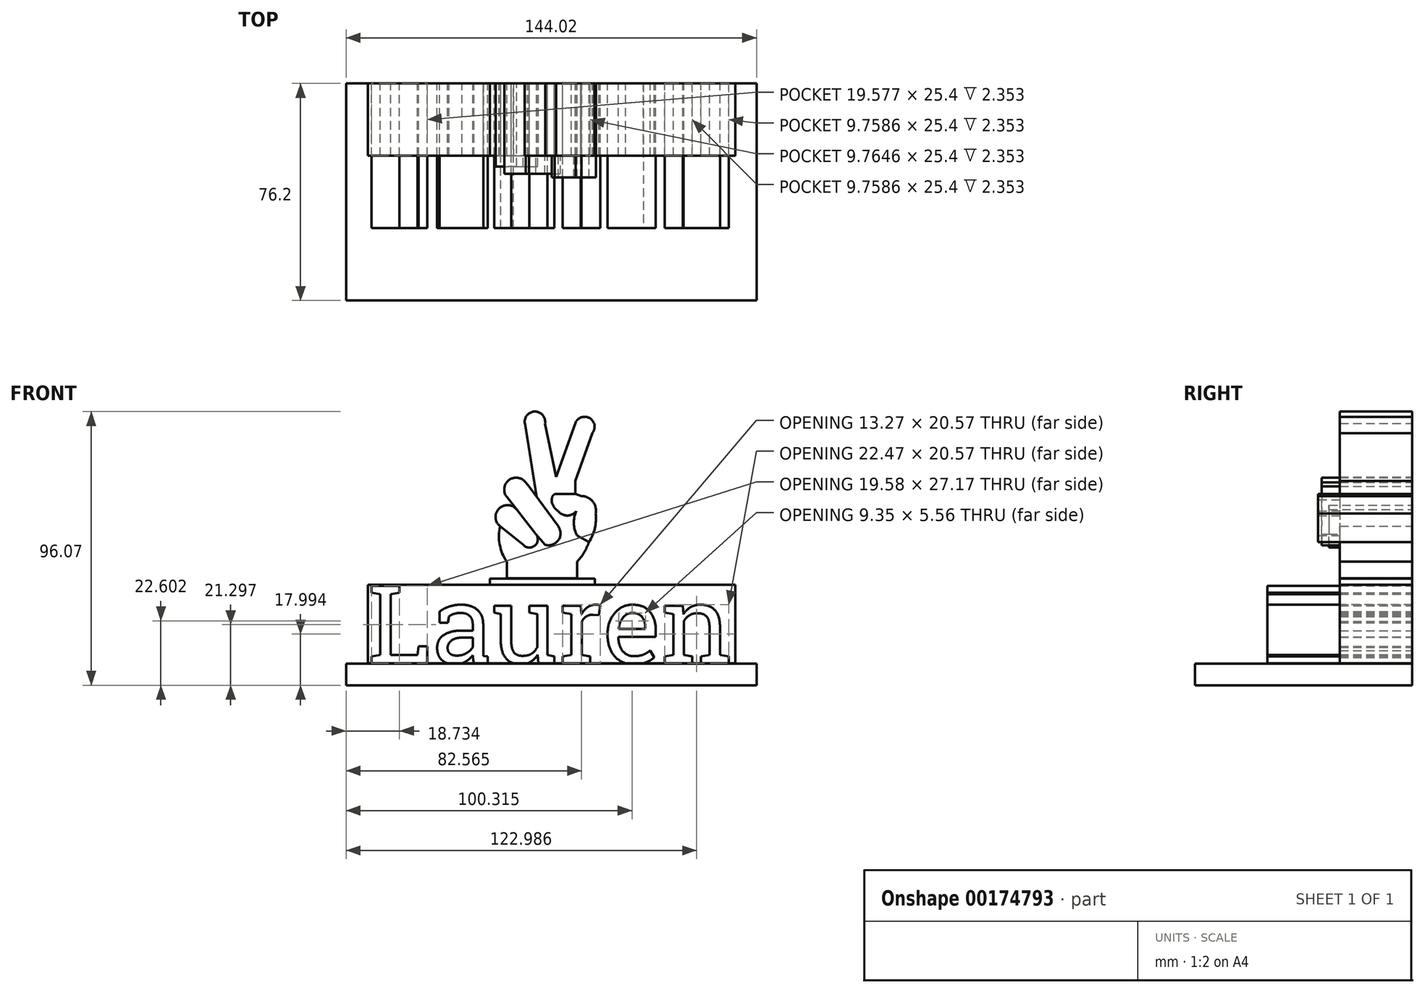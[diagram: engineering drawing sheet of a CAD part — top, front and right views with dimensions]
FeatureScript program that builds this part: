
annotation { "Feature Type Name" : "Feature", "Feature Type Description" : "" }
export const myFeature = defineFeature(function(context is Context, id is Id, definition is map)
    precondition{}
    {
        {
            var Q0;
            Q0=qCreatedBy(makeId("Front.planeOp"),FACE);
            var sketch = newSketch(context, id + "F0", { "sketchPlane" : qUnion([Q0])});
            skLineSegment(sketch, "E0.bottom", {"start": v(64.49, 13.76) * mm, "end": v(-64.49, 13.76) * mm});
            skLineSegment(sketch, "E0.top", {"start": v(64.49, -13.76) * mm, "end": v(-64.49, -13.76) * mm});
            skLineSegment(sketch, "E0.left", {"start": v(64.49, 13.76) * mm, "end": v(64.49, -13.76) * mm});
            skLineSegment(sketch, "E0.right", {"start": v(-64.49, 13.76) * mm, "end": v(-64.49, -13.76) * mm});
            skPoint(sketch, "E0.middle", {"position": v(0, 0) * mm});
            skText(sketch, "E1", { "text": "Lauren", "fontName": "RobotoSlab-Regular.ttf"});
            const initialGuessF0  = {"E1": [-0.06449, -0.01376, 1, 0, 0.02752]};
            skSetInitialGuess(sketch, initialGuessF0);
            skSolve(sketch);
        }
        {
            var Q0;
            Q0=makeQuery(id+"F0.imprint","IMPRINT",FACE,{"disambiguationData":[TD([[makeQuery(id+"F0.imprint","IMPRINT",EDGE,{"derivedFrom":sQuery(id+"F0.wireOp",EDGE,"E1.sketch_text.stroke-0")}),-1.0]])]});
            var Q1;
            Q1=makeQuery(id+"F0.imprint","IMPRINT",FACE,{"disambiguationData":[TD([[makeQuery(id+"F0.imprint","IMPRINT",EDGE,{"derivedFrom":sQuery(id+"F0.wireOp",EDGE,"E1.sketch_text.stroke-16")}),-1.0]])]});
            var Q2;
            {var subQ5=sQuery(id+"F0.wireOp",EDGE,"E1.sketch_text.stroke-51");Q2=makeQuery(id+"F0.imprint","IMPRINT",FACE,{"disambiguationData":[TD([[makeQuery(id+"F0.imprint","IMPRINT",EDGE,{"derivedFrom":subQ5}),-1.0]])]});}
            var Q3;
            Q3=makeQuery(id+"F0.imprint","IMPRINT",FACE,{"disambiguationData":[TD([[makeQuery(id+"F0.imprint","IMPRINT",EDGE,{"derivedFrom":sQuery(id+"F0.wireOp",EDGE,"E1.sketch_text.stroke-75")}),-1.0]])]});
            var Q4;
            {var subQ4=sQuery(id+"F0.wireOp",EDGE,"E1.sketch_text.stroke-95");Q4=makeQuery(id+"F0.imprint","IMPRINT",FACE,{"disambiguationData":[TD([[makeQuery(id+"F0.imprint","IMPRINT",EDGE,{"derivedFrom":subQ4}),-1.0]])]});}
            var Q5;
            Q5=makeQuery(id+"F0.imprint","IMPRINT",FACE,{"disambiguationData":[TD([[makeQuery(id+"F0.imprint","IMPRINT",EDGE,{"derivedFrom":sQuery(id+"F0.wireOp",EDGE,"E1.sketch_text.stroke-118")}),-1.0]])]});
            extrude(context, id + "F1", {"entities" : qUnion([Q0, Q1, Q2, Q3, Q4, Q5]), "depth" : 50.8 * mm});
        }
        {
            var Q0;
            Q0=makeQuery(id+"F0.imprint","IMPRINT",FACE,{"disambiguationData":[TD([[makeQuery(id+"F0.imprint","IMPRINT",EDGE,{"derivedFrom":sQuery(id+"F0.wireOp",EDGE,"E0.bottom")}),1.0]])]});
            extrude(context, id + "F2", {"entities" : qUnion([Q0]), "depth" : 25.4 * mm});
        }
        {
            var Q0;
            Q0=qCreatedBy(makeId("Front.planeOp"),FACE);
            var sketch = newSketch(context, id + "F3", { "sketchPlane" : qUnion([Q0])});
            skLineSegment(sketch, "E2", {"start": v(-15.98, 16.07) * mm, "end": v(8.98, 16.07) * mm});
            skLineSegment(sketch, "E3", {"start": v(8.98, 16.07) * mm, "end": v(8.98, 21.88) * mm});
            skLineSegment(sketch, "E4", {"start": v(-15.75, 21.88) * mm, "end": v(-15.75, 16.07) * mm});
            skArc(sketch, "E5", {"start": v(-18.1, 34.33) * mm, "mid": v(-18.2, 27.87) * mm, "end": v(-15.75, 21.88) * mm});
            skArc(sketch, "E6", {"start": v(-12.22, 40.18) * mm, "mid": v(-18.44, 40.55) * mm, "end": v(-18.1, 34.33) * mm});
            skLineSegment(sketch, "E7", {"start": v(-18.1, 34.33) * mm, "end": v(-10.02, 27.87) * mm});
            skPoint(sketch, "E7.endSnap0", {"position": v(-18.2, 27.87) * mm});
            skLineSegment(sketch, "E8", {"start": v(-12.22, 40.18) * mm, "end": v(-5.48, 31.62) * mm});
            skArc(sketch, "E9", {"start": v(-10.02, 27.87) * mm, "mid": v(-5.92, 27.53) * mm, "end": v(-5.48, 31.62) * mm});
            skLineSegment(sketch, "E10", {"start": v(-12.22, 40.18) * mm, "end": v(-15.75, 44.65) * mm});
            skArc(sketch, "E11", {"start": v(-9.15, 49.75) * mm, "mid": v(-15.02, 50.53) * mm, "end": v(-15.75, 44.65) * mm});
            skLineSegment(sketch, "E12", {"start": v(-7.95, 48.38) * mm, "end": v(2.3, 34.34) * mm});
            skLineSegment(sketch, "E13", {"start": v(-7.95, 48.38) * mm, "end": v(-9.15, 49.75) * mm});
            skLineSegment(sketch, "E14", {"start": v(-5.48, 31.62) * mm, "end": v(-2.4, 27.87) * mm});
            skArc(sketch, "E15", {"start": v(-2.4, 27.87) * mm, "mid": v(2.31, 29.39) * mm, "end": v(2.3, 34.34) * mm});
            skArc(sketch, "E16", {"start": v(8.72, 39.66) * mm, "mid": v(7.78, 35.36) * mm, "end": v(8.98, 31.12) * mm});
            skArc(sketch, "E17", {"start": v(2.3, 39.66) * mm, "mid": v(5.51, 38.1) * mm, "end": v(8.72, 39.66) * mm});
            skArc(sketch, "E18", {"start": v(0, 43.6) * mm, "mid": v(0.66, 41.34) * mm, "end": v(2.3, 39.66) * mm});
            skArc(sketch, "E19", {"start": v(1.05, 45.65) * mm, "mid": v(0.3, 44.74) * mm, "end": v(0, 43.6) * mm});
            skLineSegment(sketch, "E20", {"start": v(1.05, 45.65) * mm, "end": v(8.46, 45.65) * mm});
            skLineSegment(sketch, "E21", {"start": v(-5.3, 44.75) * mm, "end": v(-9.4, 70.44) * mm});
            skArc(sketch, "E22", {"start": v(-2.3, 70.44) * mm, "mid": v(-5.86, 74.6) * mm, "end": v(-9.4, 70.44) * mm});
            skLineSegment(sketch, "E23", {"start": v(-2.3, 70.44) * mm, "end": v(1.62, 51.63) * mm});
            skLineSegment(sketch, "E24", {"start": v(1.62, 51.63) * mm, "end": v(8.3, 70.44) * mm});
            skArc(sketch, "E25", {"start": v(14.28, 67.02) * mm, "mid": v(13.33, 72.3) * mm, "end": v(8.3, 70.44) * mm});
            skLineSegment(sketch, "E26", {"start": v(14.28, 67.02) * mm, "end": v(8.31, 50.2) * mm});
            skLineSegment(sketch, "E27", {"start": v(8.31, 50.2) * mm, "end": v(8.31, 45.65) * mm});
            skArc(sketch, "E28", {"start": v(8.98, 21.88) * mm, "mid": v(11.37, 25.1) * mm, "end": v(13.08, 28.72) * mm});
            skArc(sketch, "E29", {"start": v(13.08, 28.72) * mm, "mid": v(15.15, 33.56) * mm, "end": v(15.47, 38.8) * mm});
            skArc(sketch, "E30", {"start": v(15.47, 38.8) * mm, "mid": v(14.41, 43.03) * mm, "end": v(10.51, 44.96) * mm});
            skLineSegment(sketch, "E31", {"start": v(10.51, 44.96) * mm, "end": v(8.46, 45.65) * mm});
            skLineSegment(sketch, "E32", {"start": v(8.98, 31.12) * mm, "end": v(13.08, 28.72) * mm});
            skSolve(sketch);
        }
        {
            var Q0;
            {var subQ6=sQuery(id+"F3.wireOp",EDGE,"E3");Q0=makeQuery(id+"F3.imprint","IMPRINT",FACE,{"disambiguationData":[TD([[makeQuery(id+"F3.imprint","IMPRINT",EDGE,{"derivedFrom":subQ6}),1.0]])]});}
            extrude(context, id + "F4", {"entities" : qUnion([Q0]), "depth" : 25.4 * mm});
        }
        {
            var Q0;
            Q0=makeQuery(id+"F3.imprint","IMPRINT",FACE,{"disambiguationData":[TD([[makeQuery(id+"F3.imprint","IMPRINT",EDGE,{"derivedFrom":sQuery(id+"F3.wireOp",EDGE,"E6")}),1.0]])]});
            extrude(context, id + "F5", {"entities" : qUnion([Q0]), "operationType" : NewBodyOperationType.ADD, "depth" : 29.2 * mm});
        }
        {
            var Q0;
            Q0=makeQuery(id+"F3.imprint","IMPRINT",FACE,{"disambiguationData":[TD([[makeQuery(id+"F3.imprint","IMPRINT",EDGE,{"derivedFrom":sQuery(id+"F3.wireOp",EDGE,"E8")}),1.0]])]});
            extrude(context, id + "F6", {"entities" : qUnion([Q0]), "operationType" : NewBodyOperationType.ADD, "depth" : 31.75 * mm});
        }
        {
            var Q0;
            Q0=makeQuery(id+"F3.imprint","IMPRINT",FACE,{"disambiguationData":[TD([[makeQuery(id+"F3.imprint","IMPRINT",EDGE,{"derivedFrom":sQuery(id+"F3.wireOp",EDGE,"E16")}),1.0]])]});
            extrude(context, id + "F7", {"entities" : qUnion([Q0]), "operationType" : NewBodyOperationType.ADD, "depth" : 33.02 * mm});
        }
        {
            var Q0;
            Q0=qCreatedBy(makeId("Front.planeOp"),FACE);
            var sketch = newSketch(context, id + "F8", { "sketchPlane" : qUnion([Q0])});
            skLineSegment(sketch, "E33", {"start": v(-15.95, 16.02) * mm, "end": v(-21.7, 16.02) * mm});
            skLineSegment(sketch, "E34", {"start": v(-21.7, 16.02) * mm, "end": v(-21.7, 13.78) * mm});
            skLineSegment(sketch, "E35", {"start": v(-21.7, 13.78) * mm, "end": v(15.15, 13.78) * mm});
            skLineSegment(sketch, "E36", {"start": v(15.15, 13.78) * mm, "end": v(15.15, 16.02) * mm});
            skLineSegment(sketch, "E37", {"start": v(15.15, 16.02) * mm, "end": v(9.2, 16.02) * mm});
            skLineSegment(sketch, "E38", {"start": v(9.2, 16.02) * mm, "end": v(-15.95, 16.02) * mm});
            skSolve(sketch);
        }
        {
            var Q0;
            Q0=makeQuery(id+"F8.imprint","IMPRINT",FACE,{"disambiguationData":[TD([[makeQuery(id+"F8.imprint","IMPRINT",EDGE,{"derivedFrom":sQuery(id+"F8.wireOp",EDGE,"E33")}),1.0]])]});
            extrude(context, id + "F9", {"entities" : qUnion([Q0]), "depth" : 25.4 * mm});
        }
        {
            var Q0;
            Q0=qCreatedBy(makeId("Front.planeOp"),FACE);
            var sketch = newSketch(context, id + "F10", { "sketchPlane" : qUnion([Q0])});
            skLineSegment(sketch, "E39", {"start": v(-64.2, -13.85) * mm, "end": v(-72.1, -13.85) * mm});
            skLineSegment(sketch, "E40", {"start": v(-72.1, -13.85) * mm, "end": v(-72.1, -21.47) * mm});
            skLineSegment(sketch, "E41", {"start": v(-72.1, -21.47) * mm, "end": v(71.9, -21.47) * mm});
            skLineSegment(sketch, "E42", {"start": v(71.9, -21.47) * mm, "end": v(71.9, -13.85) * mm});
            skLineSegment(sketch, "E43", {"start": v(71.9, -13.85) * mm, "end": v(64.29, -13.85) * mm});
            skLineSegment(sketch, "E44", {"start": v(64.29, -13.85) * mm, "end": v(-64.2, -13.85) * mm});
            skSolve(sketch);
        }
        {
            var Q0;
            Q0=makeQuery(id+"F10.imprint","IMPRINT",FACE,{"disambiguationData":[TD([[makeQuery(id+"F10.imprint","IMPRINT",EDGE,{"derivedFrom":sQuery(id+"F10.wireOp",EDGE,"E39")}),1.0]])]});
            extrude(context, id + "F11", {"entities" : qUnion([Q0]), "depth" : 76.2 * mm});
        }
    });
